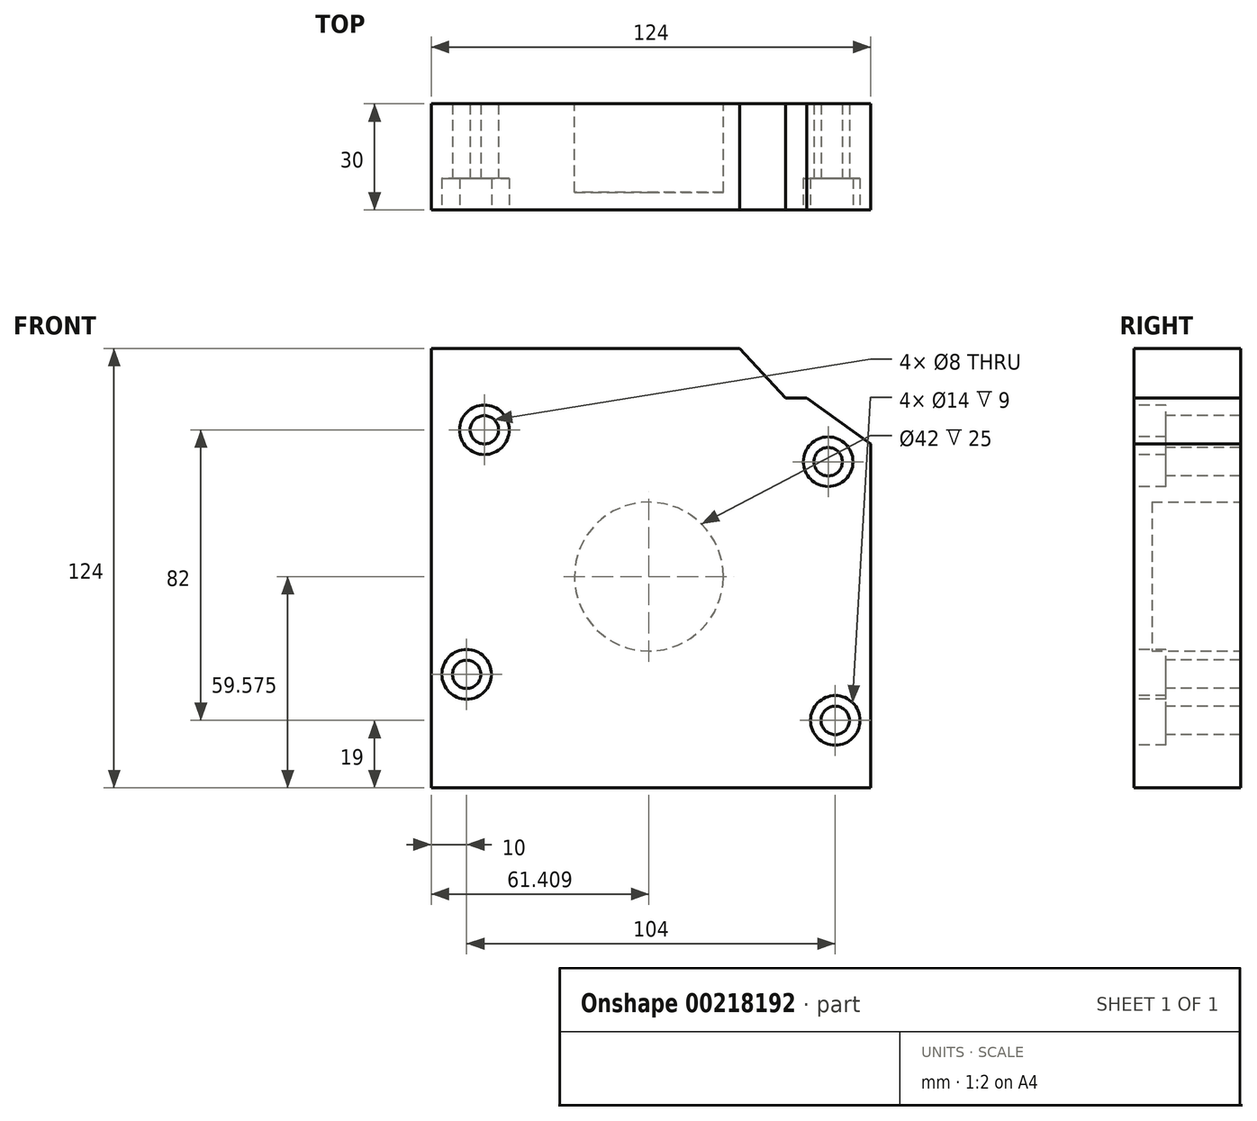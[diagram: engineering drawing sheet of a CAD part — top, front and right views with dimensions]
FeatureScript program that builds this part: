
annotation { "Feature Type Name" : "Feature", "Feature Type Description" : "" }
export const myFeature = defineFeature(function(context is Context, id is Id, definition is map)
    precondition{}
    {
        {
            var Q0;
            Q0=qCreatedBy(makeId("Front.planeOp"),FACE);
            var sketch = newSketch(context, id + "F0", { "sketchPlane" : qUnion([Q0])});
            skLineSegment(sketch, "E0.bottom", {"start": v(0, 0) * mm, "end": v(87, 0) * mm});
            skLineSegment(sketch, "E0.top", {"start": v(0, -124) * mm, "end": v(124, -124) * mm});
            skLineSegment(sketch, "E0.left", {"start": v(0, 0) * mm, "end": v(0, -124) * mm});
            skLineSegment(sketch, "E0.right", {"start": v(124, -27) * mm, "end": v(124, -124) * mm});
            skPoint(sketch, "E1", {"position": v(87, 0) * mm});
            skPoint(sketch, "E2", {"position": v(100, -14) * mm});
            skPoint(sketch, "E3", {"position": v(106, -14.07) * mm});
            skPoint(sketch, "E4", {"position": v(124, -27) * mm});
            skLineSegment(sketch, "E5", {"start": v(124, -27) * mm, "end": v(106, -14.07) * mm});
            skLineSegment(sketch, "E6", {"start": v(106, -14.07) * mm, "end": v(100, -14) * mm});
            skLineSegment(sketch, "E7", {"start": v(100, -14) * mm, "end": v(87, 0) * mm});
            skPoint(sketch, "E8.orphan", {"position": v(124, 0) * mm});
            skSolve(sketch);
        }
        {
            var Q0;
            Q0=makeQuery(id+"F0.imprint","IMPRINT",FACE,{"disambiguationData":[TD([[makeQuery(id+"F0.imprint","IMPRINT",EDGE,{"derivedFrom":sQuery(id+"F0.wireOp",EDGE,"E0.bottom")}),-1.0]])]});
            extrude(context, id + "F1", {"entities" : qUnion([Q0]), "depth" : 30 * mm});
        }
        {
            var Q0;
            Q0=makeQuery(id+"F1.opExtrude","CAP_FACE",FACE,{"disambiguationData":[OSD([sQuery(id+"F0.wireOp",EDGE,"E0.bottom"),sQuery(id+"F0.wireOp",EDGE,"E0.top"),sQuery(id+"F0.wireOp",EDGE,"E0.left"),sQuery(id+"F0.wireOp",EDGE,"E0.right"),sQuery(id+"F0.wireOp",EDGE,"E5"),sQuery(id+"F0.wireOp",EDGE,"E6"),sQuery(id+"F0.wireOp",EDGE,"E7")])],"isStart":false});
            var sketch = newSketch(context, id + "F2", { "sketchPlane" : qUnion([Q0])});
            skPoint(sketch, "E9", {"position": v(15, -23) * mm});
            skPoint(sketch, "E10", {"position": v(10, -92) * mm});
            skPoint(sketch, "E11", {"position": v(112, -32) * mm});
            skPoint(sketch, "E12", {"position": v(114, -105) * mm});
            skSolve(sketch);
        }
        {
            var Q0;
            Q0=sQuery(id+"F2.wireOp",VERTEX,"E9");
            var Q1;
            Q1=sQuery(id+"F2.wireOp",VERTEX,"E10");
            var Q2;
            Q2=sQuery(id+"F2.wireOp",VERTEX,"E11");
            var Q3;
            Q3=sQuery(id+"F2.wireOp",VERTEX,"E12");
            var Q4;
            Q4=makeQuery(id+"F1.opExtrude","SWEPT_BODY",BODY,{"disambiguationData":[OSD([sQuery(id+"F0.wireOp",EDGE,"E0.bottom"),sQuery(id+"F0.wireOp",EDGE,"E0.top"),sQuery(id+"F0.wireOp",EDGE,"E0.left"),sQuery(id+"F0.wireOp",EDGE,"E0.right"),sQuery(id+"F0.wireOp",EDGE,"E5"),sQuery(id+"F0.wireOp",EDGE,"E6"),sQuery(id+"F0.wireOp",EDGE,"E7")])]});
            hole(context, id + "F3", {"style" : HoleStyle.C_BORE, "endStyle" : HoleEndStyle.BLIND, "holeDiameter" : 8 * mm, "cBoreDiameter" : 14 * mm, "cBoreDepth" : 9 * mm, "holeDepth" : 45 * mm, "startFromSketch" : true, "locations" : qUnion([Q0, Q1, Q2, Q3]), "scope" : qUnion([Q4])});
        }
        {
            var Q0;
            Q0=makeQuery(id+"F1.opExtrude","CAP_FACE",FACE,{"disambiguationData":[OSD([sQuery(id+"F0.wireOp",EDGE,"E0.bottom"),sQuery(id+"F0.wireOp",EDGE,"E0.top"),sQuery(id+"F0.wireOp",EDGE,"E0.left"),sQuery(id+"F0.wireOp",EDGE,"E0.right"),sQuery(id+"F0.wireOp",EDGE,"E5"),sQuery(id+"F0.wireOp",EDGE,"E6"),sQuery(id+"F0.wireOp",EDGE,"E7")])],"isStart":true});
            var sketch = newSketch(context, id + "F4", { "sketchPlane" : qUnion([Q0])});
            skPoint(sketch, "E13", {"position": v(-62, -63.97) * mm});
            skSolve(sketch);
        }
        {
            var Q0;
            {var subQ6=sQuery(id+"F0.wireOp",EDGE,"E0.bottom");Q0=makeQuery(id+"F4.imprint","IMPRINT",FACE,{"disambiguationData":[TD([[makeQuery(id+"F4.imprint","IMPRINT",EDGE,{"derivedFrom":makeQuery(id+"F1.opExtrude","CAP_EDGE",EDGE,{"disambiguationData":[OSD([subQ6])],"isStart":true})}),1.0]])]});}
            var sketch = newSketch(context, id + "F5", { "sketchPlane" : qUnion([Q0])});
            skCircle(sketch, "E14", {"center": v(-61.4, -64.43) * mm, "radius": 21 * mm});
            skSolve(sketch);
        }
        {
            var Q0;
            Q0=makeQuery(id+"F5.imprint","IMPRINT",FACE,{"disambiguationData":[TD([[makeQuery(id+"F5.imprint","IMPRINT",EDGE,{"derivedFrom":sQuery(id+"F5.wireOp",EDGE,"E14")}),1.0]])]});
            extrude(context, id + "F6", {"entities" : qUnion([Q0]), "operationType" : NewBodyOperationType.REMOVE, "oppositeDirection" : true, "depth" : 25 * mm});
        }
    });
